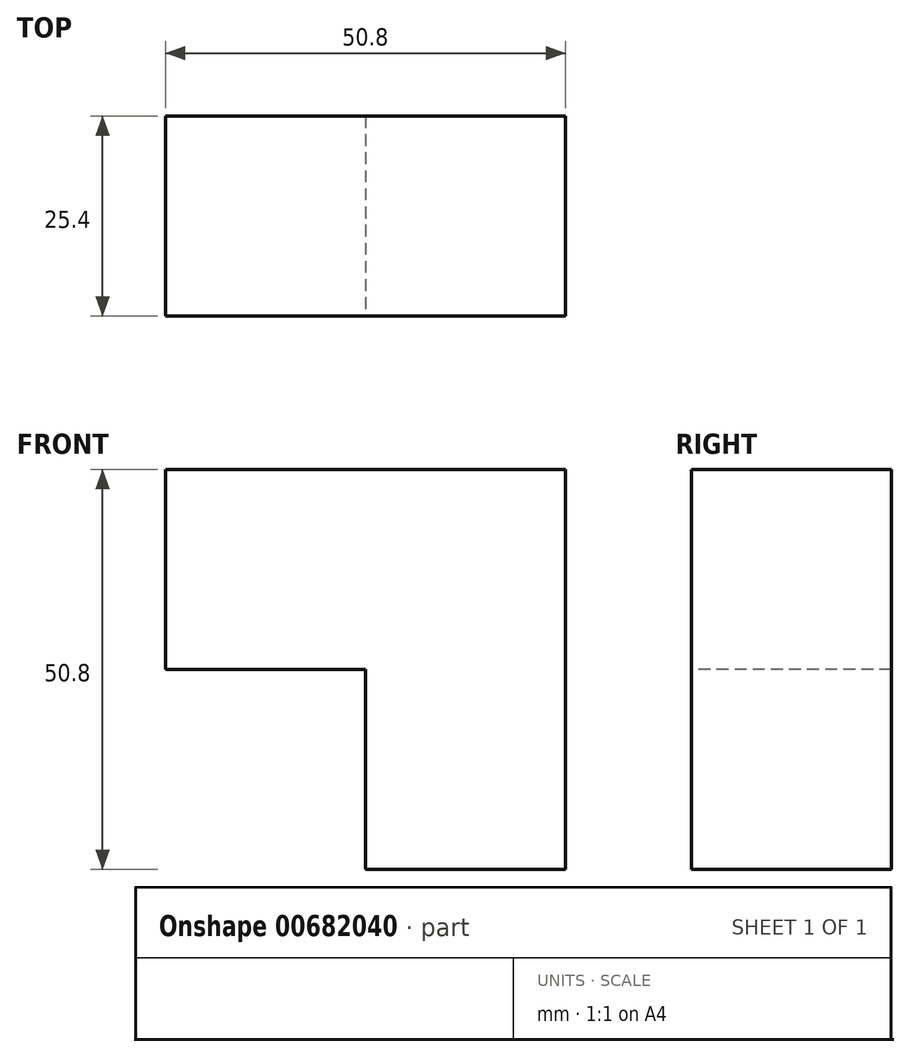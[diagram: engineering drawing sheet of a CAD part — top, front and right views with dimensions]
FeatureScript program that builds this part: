
annotation { "Feature Type Name" : "Feature", "Feature Type Description" : "" }
export const myFeature = defineFeature(function(context is Context, id is Id, definition is map)
    precondition{}
    {
        {
            var Q0;
            Q0=qCreatedBy(makeId("Front.planeOp"),FACE);
            var sketch = newSketch(context, id + "F0", { "sketchPlane" : qUnion([Q0])});
            skLineSegment(sketch, "E0", {"start": v(-50.8, 39.25) * mm, "end": v(-50.8, -11.55) * mm});
            skLineSegment(sketch, "E1", {"start": v(-50.8, -11.55) * mm, "end": v(0, -11.55) * mm});
            skLineSegment(sketch, "E2", {"start": v(-50.8, 39.25) * mm, "end": v(0, 39.25) * mm});
            skLineSegment(sketch, "E3", {"start": v(0, 39.25) * mm, "end": v(0, -11.55) * mm});
            skSolve(sketch);
        }
        {
            var Q0;
            Q0 = qSketchRegion(id + "F0", true);
            extrude(context, id + "F1", {"entities" : qUnion([Q0]), "depth" : 25.4 * mm, "offsetDistance" : 25.4 * mm});
        }
        {
            var Q0;
            Q0=makeQuery(id+"F1.opExtrude","CAP_FACE",FACE,{"disambiguationData":[OSD([sQuery(id+"F0.wireOp",EDGE,"E0"),sQuery(id+"F0.wireOp",EDGE,"E1"),sQuery(id+"F0.wireOp",EDGE,"E2"),sQuery(id+"F0.wireOp",EDGE,"E3")])],"isStart":false});
            var sketch = newSketch(context, id + "F2", { "sketchPlane" : qUnion([Q0])});
            skLineSegment(sketch, "E4", {"start": v(-50.8, 13.85) * mm, "end": v(-25.4, 13.85) * mm});
            skLineSegment(sketch, "E5", {"start": v(-25.4, 13.85) * mm, "end": v(-25.4, -11.55) * mm});
            skLineSegment(sketch, "E6", {"start": v(-50.8, 13.85) * mm, "end": v(-50.8, -11.55) * mm});
            skLineSegment(sketch, "E7", {"start": v(-50.8, -11.55) * mm, "end": v(-25.4, -11.55) * mm});
            skSolve(sketch);
        }
        {
            var Q0;
            Q0=makeQuery(id+"F2.imprint","IMPRINT",FACE,{"disambiguationData":[TD([[makeQuery(id+"F2.imprint","IMPRINT",EDGE,{"derivedFrom":sQuery(id+"F2.wireOp",EDGE,"E4")}),-1.0]])]});
            extrude(context, id + "F3", {"entities" : qUnion([Q0]), "operationType" : NewBodyOperationType.REMOVE, "oppositeDirection" : true, "depth" : 25.4 * mm, "offsetDistance" : 25.4 * mm});
        }
    });
